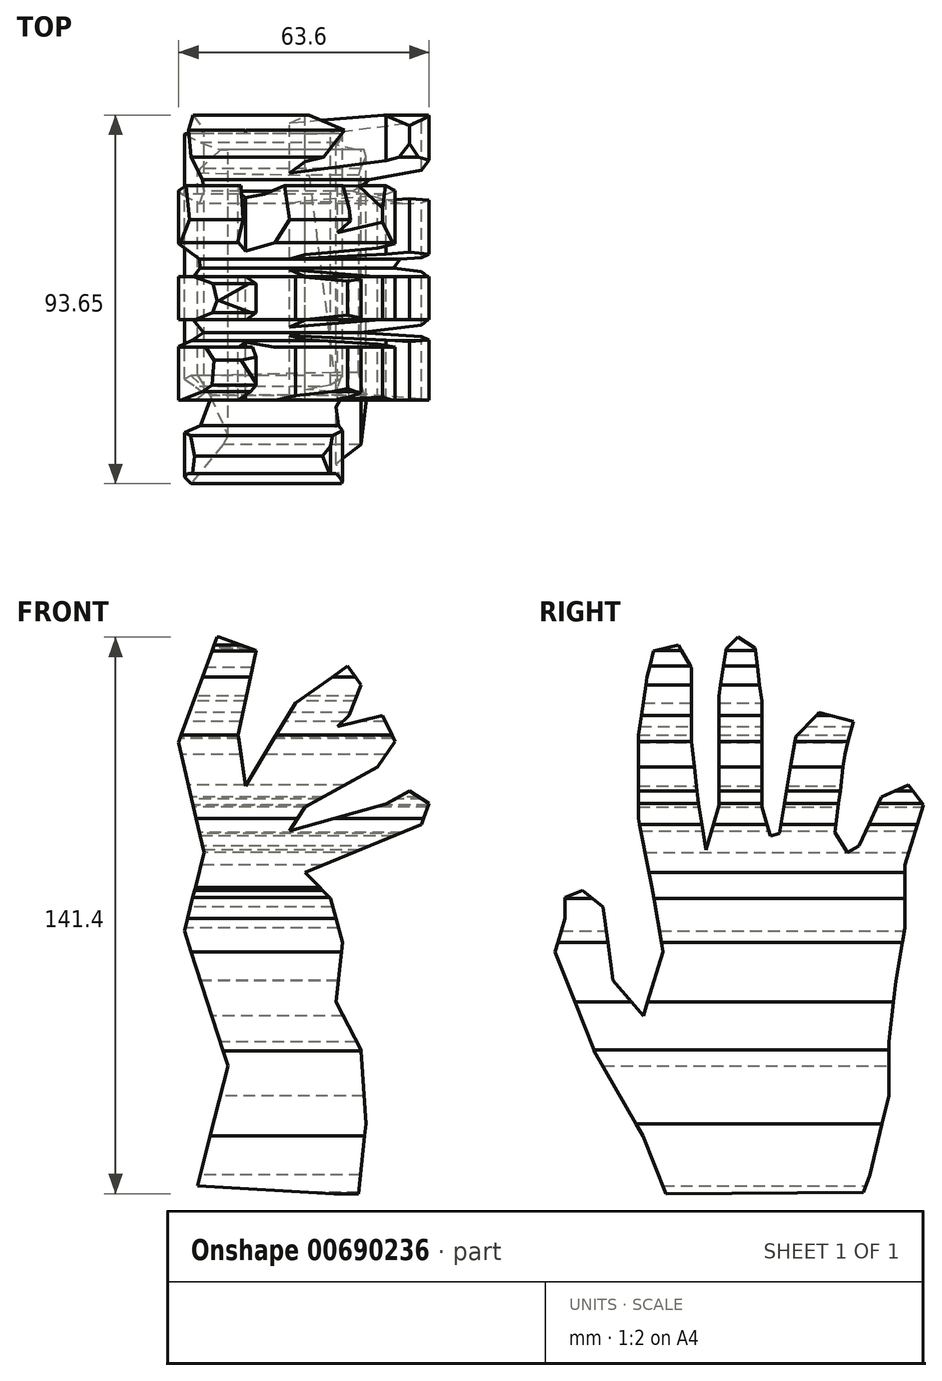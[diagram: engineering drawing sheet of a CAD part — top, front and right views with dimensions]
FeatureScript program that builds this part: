
annotation { "Feature Type Name" : "Feature", "Feature Type Description" : "" }
export const myFeature = defineFeature(function(context is Context, id is Id, definition is map)
    precondition{}
    {
        {
            var Q0;
            Q0=qCreatedBy(makeId("Front.planeOp"),FACE);
            var sketch = newSketch(context, id + "F0", { "sketchPlane" : qUnion([Q0])});
            skLineSegment(sketch, "E0", {"start": v(-27.38, -70.88) * mm, "end": v(-19.63, -40.47) * mm});
            skLineSegment(sketch, "E1", {"start": v(-19.63, -40.47) * mm, "end": v(-30.7, -6.18) * mm});
            skLineSegment(sketch, "E2", {"start": v(-30.7, -6.18) * mm, "end": v(-25.72, 13.73) * mm});
            skLineSegment(sketch, "E3", {"start": v(-25.72, 13.73) * mm, "end": v(-32.17, 41.76) * mm});
            skLineSegment(sketch, "E4", {"start": v(-32.17, 41.76) * mm, "end": v(-22.4, 68.67) * mm});
            skLineSegment(sketch, "E5", {"start": v(-22.4, 68.67) * mm, "end": v(-12.5, 65.08) * mm});
            skLineSegment(sketch, "E6", {"start": v(-12.5, 65.08) * mm, "end": v(-17.05, 43.6) * mm});
            skLineSegment(sketch, "E7", {"start": v(-17.05, 43.6) * mm, "end": v(-15.2, 30.7) * mm});
            skLineSegment(sketch, "E8", {"start": v(-15.2, 30.7) * mm, "end": v(-2.49, 51.71) * mm});
            skLineSegment(sketch, "E9", {"start": v(-2.49, 51.71) * mm, "end": v(10.78, 61.11) * mm});
            skLineSegment(sketch, "E10", {"start": v(10.78, 61.11) * mm, "end": v(14.14, 56.38) * mm});
            skLineSegment(sketch, "E11", {"start": v(14.14, 56.38) * mm, "end": v(11.15, 48.58) * mm});
            skLineSegment(sketch, "E12", {"start": v(11.15, 48.58) * mm, "end": v(8.2, 45.81) * mm});
            skLineSegment(sketch, "E13", {"start": v(8.2, 45.81) * mm, "end": v(19.63, 48.58) * mm});
            skLineSegment(sketch, "E14", {"start": v(19.63, 48.58) * mm, "end": v(22.77, 41.94) * mm});
            skLineSegment(sketch, "E15", {"start": v(22.77, 41.94) * mm, "end": v(18.34, 35.49) * mm});
            skLineSegment(sketch, "E16", {"start": v(18.34, 35.49) * mm, "end": v(0, 25.35) * mm});
            skLineSegment(sketch, "E17", {"start": v(0, 25.35) * mm, "end": v(-3.96, 19.27) * mm});
            skLineSegment(sketch, "E18", {"start": v(-3.96, 19.27) * mm, "end": v(20.56, 26.09) * mm});
            skLineSegment(sketch, "E19", {"start": v(20.56, 26.09) * mm, "end": v(26.45, 29.4) * mm});
            skLineSegment(sketch, "E20", {"start": v(26.45, 29.4) * mm, "end": v(31.43, 26.27) * mm});
            skLineSegment(sketch, "E21", {"start": v(31.43, 26.27) * mm, "end": v(29.59, 20.92) * mm});
            skLineSegment(sketch, "E22", {"start": v(29.59, 20.92) * mm, "end": v(0, 8.76) * mm});
            skLineSegment(sketch, "E23", {"start": v(0, 8.76) * mm, "end": v(6.36, 2.12) * mm});
            skLineSegment(sketch, "E24", {"start": v(6.36, 2.12) * mm, "end": v(9.5, -9.13) * mm});
            skLineSegment(sketch, "E25", {"start": v(9.5, -9.13) * mm, "end": v(7.84, -24.24) * mm});
            skLineSegment(sketch, "E26", {"start": v(7.84, -24.24) * mm, "end": v(14.1, -36.41) * mm});
            skLineSegment(sketch, "E27", {"start": v(14.1, -36.41) * mm, "end": v(15.4, -55.21) * mm});
            skLineSegment(sketch, "E28", {"start": v(15.4, -55.21) * mm, "end": v(13.55, -73.28) * mm});
            skLineSegment(sketch, "E29", {"start": v(13.55, -73.28) * mm, "end": v(-27.38, -70.88) * mm});
            skSolve(sketch);
        }
        {
            var Q0;
            Q0 = qSketchRegion(id + "F0", true);
            extrude(context, id + "F1", {"entities" : qUnion([Q0]), "endBound" : BoundingType.SYMMETRIC, "depth" : 101.6 * mm, "offsetDistance" : 25.4 * mm});
        }
        {
            var Q0;
            Q0=qCreatedBy(makeId("Right.planeOp"),FACE);
            var sketch = newSketch(context, id + "F2", { "sketchPlane" : qUnion([Q0])});
            skLineSegment(sketch, "E30", {"start": v(-22.58, -72.91) * mm, "end": v(-28.48, -58.16) * mm});
            skLineSegment(sketch, "E31", {"start": v(-28.48, -58.16) * mm, "end": v(-40.83, -36.6) * mm});
            skLineSegment(sketch, "E32", {"start": v(-40.83, -36.6) * mm, "end": v(-50.79, -11.52) * mm});
            skLineSegment(sketch, "E33", {"start": v(-50.79, -11.52) * mm, "end": v(-48.2, -3.04) * mm});
            skLineSegment(sketch, "E34", {"start": v(-48.2, -3.04) * mm, "end": v(-48.2, 2.3) * mm});
            skLineSegment(sketch, "E35", {"start": v(-48.2, 2.3) * mm, "end": v(-43.78, 4.15) * mm});
            skLineSegment(sketch, "E36", {"start": v(-43.78, 4.15) * mm, "end": v(-38.62, 0) * mm});
            skLineSegment(sketch, "E37", {"start": v(-38.62, 0) * mm, "end": v(-36.04, -18.71) * mm});
            skLineSegment(sketch, "E38", {"start": v(-36.04, -18.71) * mm, "end": v(-28.3, -27.75) * mm});
            skLineSegment(sketch, "E39", {"start": v(-28.3, -27.75) * mm, "end": v(-23.32, -11.52) * mm});
            skLineSegment(sketch, "E40", {"start": v(-23.32, -11.52) * mm, "end": v(-26.09, 4.89) * mm});
            skLineSegment(sketch, "E41", {"start": v(-26.09, 4.89) * mm, "end": v(-29.59, 22.4) * mm});
            skLineSegment(sketch, "E42", {"start": v(-29.59, 22.4) * mm, "end": v(-29.59, 43.6) * mm});
            skLineSegment(sketch, "E43", {"start": v(-29.59, 43.6) * mm, "end": v(-27.38, 58.35) * mm});
            skLineSegment(sketch, "E44", {"start": v(-27.38, 58.35) * mm, "end": v(-25.72, 64.99) * mm});
            skLineSegment(sketch, "E45", {"start": v(-25.72, 64.99) * mm, "end": v(-19.45, 66.46) * mm});
            skLineSegment(sketch, "E46", {"start": v(-19.45, 66.46) * mm, "end": v(-16.13, 60.74) * mm});
            skLineSegment(sketch, "E47", {"start": v(-16.13, 60.74) * mm, "end": v(-16.13, 42.68) * mm});
            skLineSegment(sketch, "E48", {"start": v(-16.13, 42.68) * mm, "end": v(-14.47, 27.38) * mm});
            skLineSegment(sketch, "E49", {"start": v(-14.47, 27.38) * mm, "end": v(-12.44, 14.47) * mm});
            skLineSegment(sketch, "E50", {"start": v(-12.44, 14.47) * mm, "end": v(-9.13, 25.72) * mm});
            skLineSegment(sketch, "E51", {"start": v(-9.13, 25.72) * mm, "end": v(-9.13, 53.56) * mm});
            skLineSegment(sketch, "E52", {"start": v(-9.13, 53.56) * mm, "end": v(-7.28, 65.54) * mm});
            skLineSegment(sketch, "E53", {"start": v(-7.28, 65.54) * mm, "end": v(-4.33, 68.49) * mm});
            skLineSegment(sketch, "E54", {"start": v(-4.33, 68.49) * mm, "end": v(0, 65.72) * mm});
            skLineSegment(sketch, "E55", {"start": v(0, 65.72) * mm, "end": v(1.75, 52.26) * mm});
            skLineSegment(sketch, "E56", {"start": v(1.75, 52.26) * mm, "end": v(1.75, 25.35) * mm});
            skLineSegment(sketch, "E57", {"start": v(1.75, 25.35) * mm, "end": v(3.96, 17.97) * mm});
            skLineSegment(sketch, "E58", {"start": v(3.96, 17.97) * mm, "end": v(6.2, 18.64) * mm});
            skLineSegment(sketch, "E59", {"start": v(6.2, 18.64) * mm, "end": v(10.42, 43.23) * mm});
            skLineSegment(sketch, "E60", {"start": v(10.42, 43.23) * mm, "end": v(16.32, 49.31) * mm});
            skLineSegment(sketch, "E61", {"start": v(16.32, 49.31) * mm, "end": v(24.98, 47.1) * mm});
            skLineSegment(sketch, "E62", {"start": v(24.98, 47.1) * mm, "end": v(22.82, 38.66) * mm});
            skLineSegment(sketch, "E63", {"start": v(22.82, 38.66) * mm, "end": v(20.37, 18.9) * mm});
            skLineSegment(sketch, "E64", {"start": v(20.37, 18.9) * mm, "end": v(23.5, 13.73) * mm});
            skLineSegment(sketch, "E65", {"start": v(23.5, 13.73) * mm, "end": v(26.4, 15.49) * mm});
            skLineSegment(sketch, "E66", {"start": v(26.4, 15.49) * mm, "end": v(32.17, 27.93) * mm});
            skLineSegment(sketch, "E67", {"start": v(32.17, 27.93) * mm, "end": v(39, 30.88) * mm});
            skLineSegment(sketch, "E68", {"start": v(39, 30.88) * mm, "end": v(42.86, 25.9) * mm});
            skLineSegment(sketch, "E69", {"start": v(42.86, 25.9) * mm, "end": v(38.07, 10.6) * mm});
            skLineSegment(sketch, "E70", {"start": v(38.07, 10.6) * mm, "end": v(38.07, -5.44) * mm});
            skLineSegment(sketch, "E71", {"start": v(38.07, -5.44) * mm, "end": v(35.86, -18.9) * mm});
            skLineSegment(sketch, "E72", {"start": v(35.86, -18.9) * mm, "end": v(34.01, -34.38) * mm});
            skLineSegment(sketch, "E73", {"start": v(34.01, -34.38) * mm, "end": v(34.01, -48.02) * mm});
            skLineSegment(sketch, "E74", {"start": v(34.01, -48.02) * mm, "end": v(29.22, -68.12) * mm});
            skLineSegment(sketch, "E75", {"start": v(29.22, -68.12) * mm, "end": v(27.56, -72.54) * mm});
            skLineSegment(sketch, "E76", {"start": v(27.56, -72.54) * mm, "end": v(-22.58, -72.91) * mm});
            skSolve(sketch);
        }
        {
            var Q0;
            Q0 = qSketchRegion(id + "F2", true);
            extrude(context, id + "F3", {"entities" : qUnion([Q0]), "operationType" : NewBodyOperationType.INTERSECT, "endBound" : BoundingType.SYMMETRIC, "depth" : 177.8 * mm, "offsetDistance" : 25.4 * mm});
        }
    });
